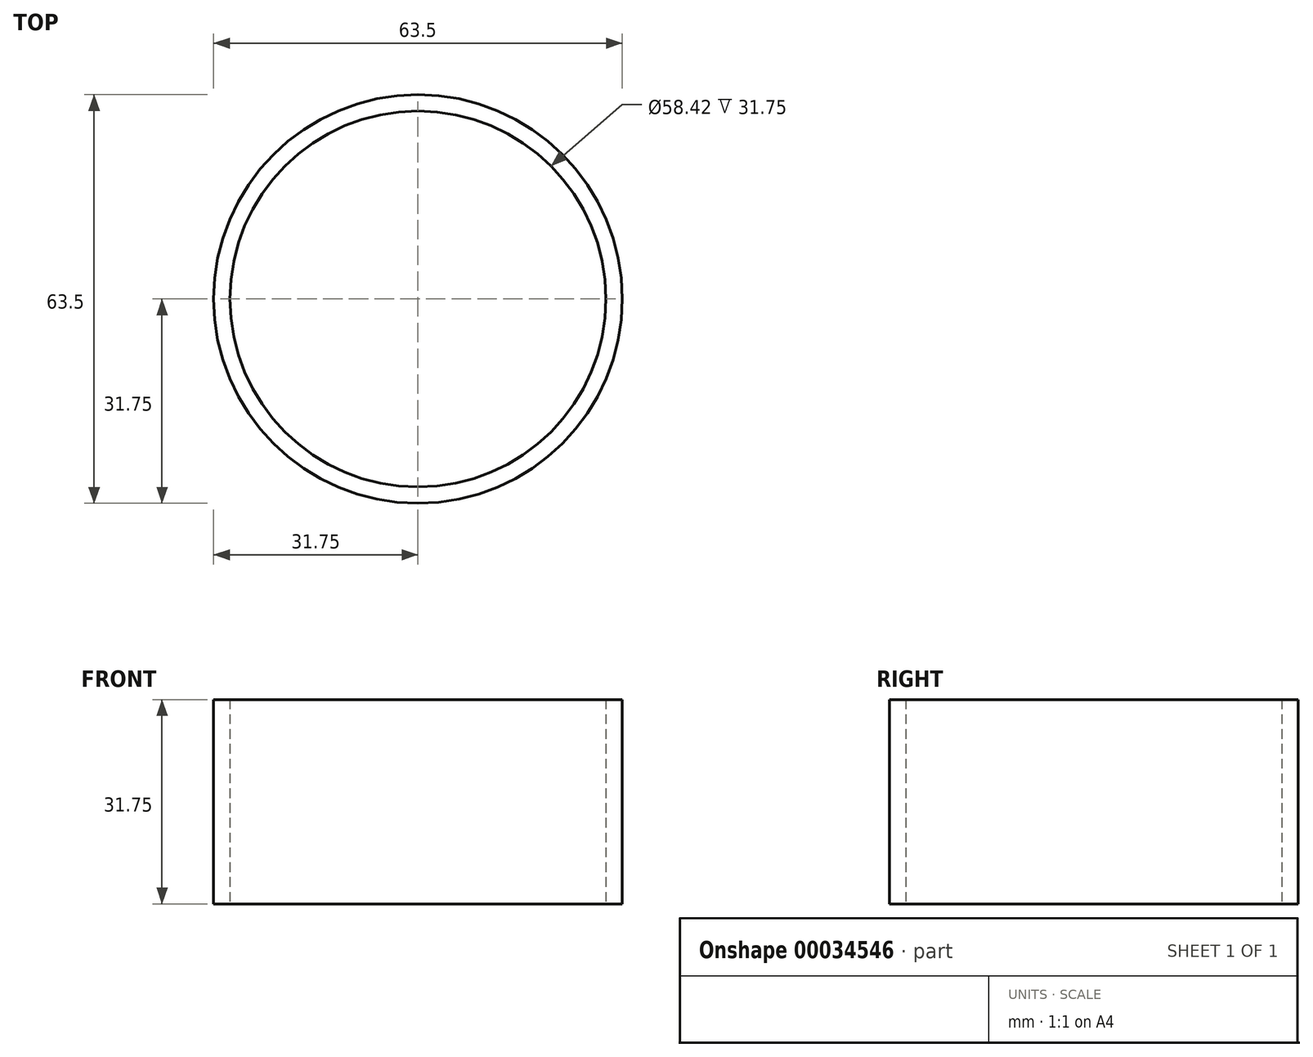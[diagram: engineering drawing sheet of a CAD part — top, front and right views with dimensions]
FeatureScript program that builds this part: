
annotation { "Feature Type Name" : "Feature", "Feature Type Description" : "" }
export const myFeature = defineFeature(function(context is Context, id is Id, definition is map)
    precondition{}
    {
        {
            var Q0;
            Q0=qCreatedBy(makeId("Top.planeOp"),FACE);
            var sketch = newSketch(context, id + "F0", { "sketchPlane" : qUnion([Q0])});
            skCircle(sketch, "E0", {"center": v(0, 0) * mm, "radius": 29.21 * mm});
            skCircle(sketch, "E1.0", {"center": v(0, 0) * mm, "radius": 31.75 * mm});
            skSolve(sketch);
        }
        {
            var Q0;
            Q0=makeQuery(id+"F0.imprint","IMPRINT",FACE,{"disambiguationData":[TD([[makeQuery(id+"F0.imprint","IMPRINT",EDGE,{"derivedFrom":sQuery(id+"F0.wireOp",EDGE,"E0")}),-1.0]])]});
            extrude(context, id + "F1", {"entities" : qUnion([Q0]), "depth" : 31.75 * mm});
        }
    });
